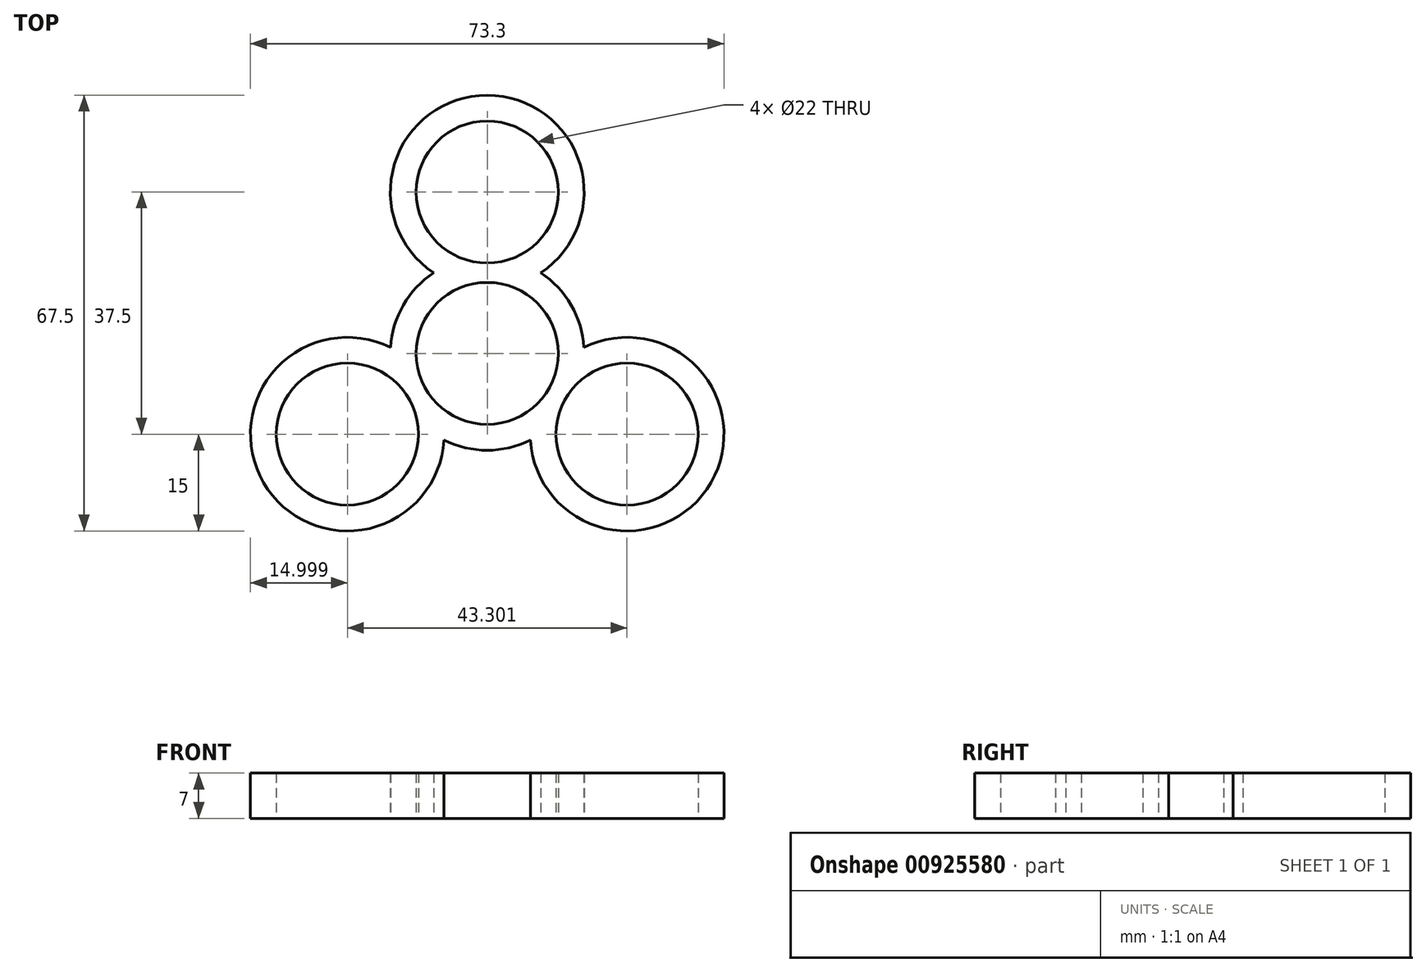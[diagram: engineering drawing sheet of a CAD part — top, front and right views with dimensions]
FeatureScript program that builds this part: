
annotation { "Feature Type Name" : "Feature", "Feature Type Description" : "" }
export const myFeature = defineFeature(function(context is Context, id is Id, definition is map)
    precondition{}
    {
        {
            var Q0;
            Q0=qCreatedBy(makeId("Top.planeOp"),FACE);
            var sketch = newSketch(context, id + "F0", { "sketchPlane" : qUnion([Q0])});
            skArc(sketch, "E0", {"start": v(9.53, 5.5) * mm, "mid": v(0, 11) * mm, "end": v(-9.53, 5.5) * mm});
            skCircle(sketch, "E1", {"center": v(0, 25) * mm, "radius": 11 * mm});
            skArc(sketch, "E2", {"start": v(-8.3, 12.5) * mm, "mid": v(-10.93, 10.27) * mm, "end": v(-13, 7.5) * mm});
            skArc(sketch, "E3.trimOffspring", {"start": v(8.3, 12.5) * mm, "mid": v(0, 40) * mm, "end": v(-8.3, 12.5) * mm});
            skArc(sketch, "E4.trimOffspring", {"start": v(13, 7.5) * mm, "mid": v(10.93, 10.27) * mm, "end": v(8.3, 12.5) * mm});
            skCircle(sketch, "E5.1.0", {"center": v(-21.65, -12.5) * mm, "radius": 11 * mm});
            skArc(sketch, "E5.1.1", {"start": v(-14.97, 0.93) * mm, "mid": v(-34.64, -20) * mm, "end": v(-6.68, -13.43) * mm});
            skArc(sketch, "E5.1.2", {"start": v(-6.68, -13.43) * mm, "mid": v(-3.43, -14.6) * mm, "end": v(0, -15) * mm});
            skArc(sketch, "E5.1.3", {"start": v(-9.53, 5.5) * mm, "mid": v(-9.53, -5.5) * mm, "end": v(0, -11) * mm});
            skArc(sketch, "E5.1.4", {"start": v(-13, 7.5) * mm, "mid": v(-14.36, 4.33) * mm, "end": v(-14.97, 0.93) * mm});
            skCircle(sketch, "E5.2.0", {"center": v(21.65, -12.5) * mm, "radius": 11 * mm});
            skArc(sketch, "E5.2.1", {"start": v(6.68, -13.43) * mm, "mid": v(34.64, -20) * mm, "end": v(14.97, 0.93) * mm});
            skArc(sketch, "E5.2.2", {"start": v(14.97, 0.93) * mm, "mid": v(14.36, 4.33) * mm, "end": v(13, 7.5) * mm});
            skArc(sketch, "E5.2.3", {"start": v(0, -11) * mm, "mid": v(9.53, -5.5) * mm, "end": v(9.53, 5.5) * mm});
            skArc(sketch, "E5.2.4", {"start": v(0, -15) * mm, "mid": v(3.43, -14.6) * mm, "end": v(6.68, -13.43) * mm});
            skSolve(sketch);
        }
        {
            var Q0;
            Q0 = qSketchRegion(id + "F0", true);
            extrude(context, id + "F1", {"entities" : qUnion([Q0]), "depth" : 7 * mm, "offsetDistance" : 25 * mm});
        }
    });
